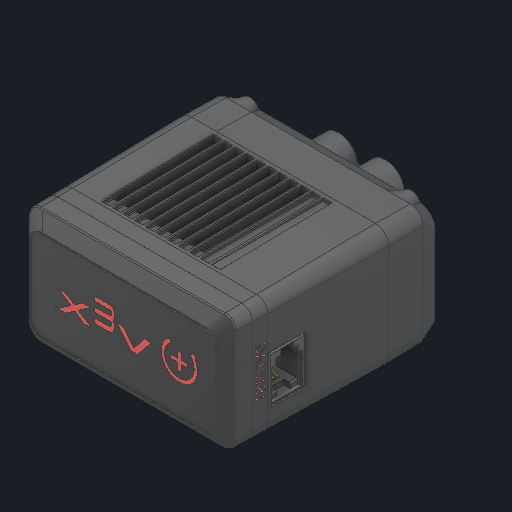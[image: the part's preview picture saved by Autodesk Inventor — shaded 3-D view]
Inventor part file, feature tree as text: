
AUTODESK INVENTOR PART (.ipt)
format: ipt  version: 2024 (Build 280153000, 153)  size: 13,035,008 bytes
history: native  units: in
note: dims shown in document units (in); Inventor stores cm internally (conversion verified against a paired STEP export)
features: other x19, sketch x2
ambient origin geometry x8: Origin, YZ Plane, XZ Plane, XY Plane, X Axis, Y Axis, Z Axis, Center Point
bodies: Solid1 (feature_tree), Solid2 (feature_tree), Solid7 (feature_tree), Solid8 (feature_tree), Solid9 (feature_tree), Solid20 (feature_tree), Solid21 (feature_tree), Solid22 (feature_tree)
feature tree (21):
  other  "V5 Motor.ipt"
  other  "Solid1::V5 Motor.ipt"
  other  "Solid2::V5 Motor.ipt"
  other  "Solid4::V5 Motor.ipt"
  other  "Solid6::V5 Motor.ipt"
  other  "Solid7::V5 Motor.ipt"
  other  "Solid8::V5 Motor.ipt"
  other  "Solid9::V5 Motor.ipt"
  other  "Solid14::V5 Motor.ipt"
  other  "Solid16::V5 Motor.ipt"
  other  "Solid17::V5 Motor.ipt"
  other  "Solid18::V5 Motor.ipt"
  other  "Solid19::V5 Motor.ipt"
  other  "Solid20::V5 Motor.ipt"
  other  "Solid21::V5 Motor.ipt"
  other  "Solid22::V5 Motor.ipt"
  other  "TaggingFeature1"
  sketch  "Sketch1"  dims[d0=0.3937in]
  sketch  "Sketch2"  dims[d4=0.0in d5=0.0in]
  other  "iInsert:1"
  other  "iInsert:2"
